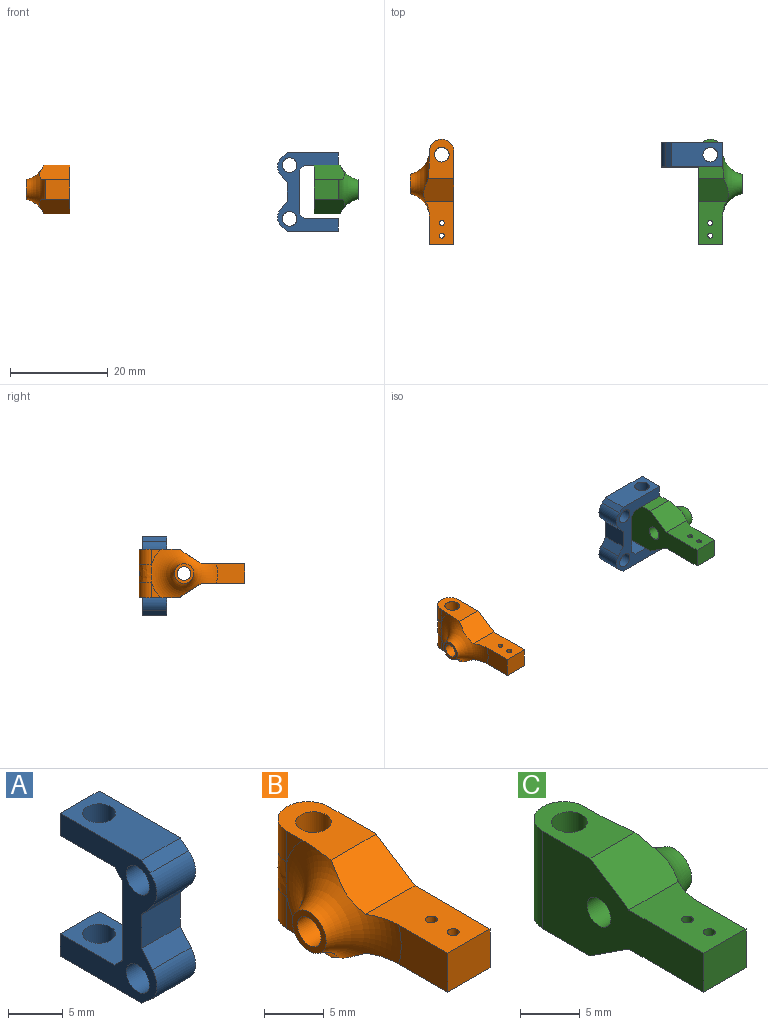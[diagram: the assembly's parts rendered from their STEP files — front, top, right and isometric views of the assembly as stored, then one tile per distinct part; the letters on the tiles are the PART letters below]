
ASSEMBLY  parts=3 mates=1
PART A: 22 faces, bbox 5x12.5x16 mm
  f0: plane 16x12.48mm, normal (1,0,0), area 82.5mm2, adj f2,f3,f4,f5,f6,f7,f8,f9
  f1: plane 16x12.48mm, normal (-1,0,0), area 82.5mm2, adj f2,f3,f4,f5,f6,f7,f8,f9
  f2: plane 5x3.79mm, normal (0,-1,0), area 18.9mm2, adj f0,f1,f14,f16
  f3: plane 9x5mm, normal (0,1,0), area 45mm2, adj f0,f1,f20,f21
  f4: plane 7x5mm, normal (0,0,-1), area 27.9mm2, adj f0,f1,f9,f11,f21
  f5: plane 10.5x5mm, normal (0,0,1), area 45.4mm2, adj f0,f1,f9,f11,f15
  f6: plane 10.5x5mm, normal (0,0,-1), area 45.4mm2, adj f0,f1,f8,f10,f12
  f7: plane 7x5mm, normal (0,0,1), area 27.9mm2, adj f0,f1,f8,f10,f20
  f8: plane 5x2.5mm, normal (0,1,0), area 12.5mm2, adj f0,f1,f6,f7
  f9: plane 5x2.5mm, normal (0,1,0), area 12.5mm2, adj f0,f1,f4,f5
  f10: cylinder r=1.5mm len=3mm, axis (0,0,1), area 23.6mm2, adj f6,f7
  f11: cylinder r=1.5mm len=3mm, axis (0,0,1), area 23.6mm2, adj f4,f5
  f12: plane 5x1.08mm, normal (0,-0.64,-0.77), area 7mm2, adj f0,f1,f6,f18
  f13: cylinder r=1.5mm len=5mm, axis (1,0,0), area 47.1mm2, adj f0,f1
  f14: plane 5x1.69mm, normal (0,-0.77,0.64), area 11mm2, adj f0,f1,f2,f18
  f15: plane 5x1.08mm, normal (0,-0.64,0.77), area 7mm2, adj f0,f1,f5,f19
  f16: plane 5x1.69mm, normal (0,-0.77,-0.64), area 11mm2, adj f0,f1,f2,f19
  f17: cylinder r=1.5mm len=5mm, axis (1,0,0), area 47.1mm2, adj f0,f1
  f18: cylinder r=2.5mm len=5mm, axis (1,0,0), area 19.6mm2, adj f0,f1,f12,f14
  f19: cylinder r=2.5mm len=5mm, axis (1,0,0), area 19.6mm2, adj f0,f1,f15,f16
  f20: plane 5x1mm, normal (0,0.71,0.71), area 7.1mm2, adj f0,f1,f3,f7
  f21: plane 5x1mm, normal (0,0.71,-0.71), area 7.1mm2, adj f0,f1,f3,f4
PART B: 20 faces, bbox 10.1x23.8x22.7 mm
  f0: plane 3.21x1.91mm, normal (-1,0,0), area 2.4mm2, adj f2,f17,f18
  f1: plane 3.21x1.91mm, normal (-1,0,0), area 2.4mm2, adj f4,f17,f18
  f2: plane 8.11x5.33mm, normal (0,0,1), area 31.3mm2, adj f0,f5,f8,f10,f17,f18
  f3: plane 5x4mm, normal (0,-1,0), area 20mm2, adj f5,f6,f9,f11
  f4: plane 8.11x5.33mm, normal (0,0,-1), area 31.3mm2, adj f1,f5,f8,f12,f17,f18
  f5: plane 19.09x10mm, normal (1,0,0), area 117.6mm2, adj f2,f3,f4,f7,f9,f10,f11,f12
  f6: plane 5.82x4mm, normal (-1,0,0), area 22.5mm2, adj f3,f9,f11,f17
  f7: cylinder r=1.4mm len=9mm, axis (-1,0,0), area 79.2mm2, adj f5,f16
  f8: cylinder r=1.5mm len=10mm, axis (0,0,1), area 94.2mm2, adj f2,f4
  f9: plane 8.89x5.88mm, normal (0,0,1), area 43.7mm2, adj f3,f5,f6,f10,f14,f15,f17
  f10: plane 6.24x4.6mm, normal (0,-0.55,0.84), area 32.6mm2, adj f2,f5,f9,f17
  f11: plane 8.89x5.88mm, normal (0,0,-1), area 43.7mm2, adj f3,f5,f6,f12,f14,f15,f17
  f12: plane 6.33x4.69mm, normal (0,-0.55,-0.84), area 32.6mm2, adj f4,f5,f11,f17
  f13: plane 3.58x0mm, normal (0,1,0), area 0mm2, adj f18,f19
  f14: cylinder r=0.5mm len=4mm, axis (0,0,1), area 12.6mm2, adj f9,f11
  f15: cylinder r=0.5mm len=4mm, axis (0,0,1), area 12.6mm2, adj f9,f11
  f16: plane 4x4mm, normal (-1,0,0), area 6.4mm2, adj f7,f17
  f17: torus R=6.9mm, axis (1,0,0), area 115.5mm2, adj f0,f1,f2,f4,f6,f9,f10,f11
  f18: cylinder r=2.5mm len=10mm, axis (0,0,-1), area 64.5mm2, adj f0,f1,f2,f4,f5,f13,f19
  f19: bspline ~6.96x2.7mm, area 13.9mm2, adj f13,f17,f18
PART C: 20 faces, bbox 10.1x23.8x22.7 mm
  f0: plane 3.21x1.91mm, normal (1,0,0), area 2.4mm2, adj f2,f17,f18
  f1: plane 3.21x1.91mm, normal (1,0,0), area 2.4mm2, adj f4,f17,f18
  f2: plane 8.11x5.33mm, normal (0,0,1), area 31.3mm2, adj f0,f5,f8,f10,f17,f18
  f3: plane 5x4mm, normal (0,-1,0), area 20mm2, adj f5,f6,f9,f11
  f4: plane 8.11x5.33mm, normal (0,0,-1), area 31.3mm2, adj f1,f5,f8,f12,f17,f18
  f5: plane 19.09x10mm, normal (-1,0,0), area 117.6mm2, adj f2,f3,f4,f7,f9,f10,f11,f12
  f6: plane 5.82x4mm, normal (1,0,0), area 22.5mm2, adj f3,f9,f11,f17
  f7: cylinder r=1.4mm len=9mm, axis (1,0,0), area 79.2mm2, adj f5,f16
  f8: cylinder r=1.5mm len=10mm, axis (0,0,1), area 94.2mm2, adj f2,f4
  f9: plane 8.89x5.88mm, normal (0,0,1), area 43.7mm2, adj f3,f5,f6,f10,f14,f15,f17
  f10: plane 6.24x4.6mm, normal (0,-0.55,0.84), area 32.6mm2, adj f2,f5,f9,f17
  f11: plane 8.89x5.88mm, normal (0,0,-1), area 43.7mm2, adj f3,f5,f6,f12,f14,f15,f17
  f12: plane 6.33x4.69mm, normal (0,-0.55,-0.84), area 32.6mm2, adj f4,f5,f11,f17
  f13: plane 3.58x0mm, normal (0,1,0), area 0mm2, adj f18,f19
  f14: cylinder r=0.5mm len=4mm, axis (0,0,1), area 12.6mm2, adj f9,f11
  f15: cylinder r=0.5mm len=4mm, axis (0,0,1), area 12.6mm2, adj f9,f11
  f16: plane 4x4mm, normal (1,0,0), area 6.4mm2, adj f7,f17
  f17: torus R=6.9mm, axis (-1,0,0), area 115.5mm2, adj f0,f1,f2,f4,f6,f9,f10,f11
  f18: cylinder r=2.5mm len=10mm, axis (0,0,-1), area 64.5mm2, adj f0,f1,f2,f4,f5,f13,f19
  f19: bspline ~6.96x2.7mm, area 13.9mm2, adj f13,f17,f18
PLACE A rot(axis=(0,0,-1),90deg) t=(32.51,9.3,-10.87)mm
PLACE B t=(-19.49,0.8,-10.37)mm
PLACE C t=(-19.49,0.8,-10.37)mm
MATE parallel A.f10 <-> C.f8  axis (0,0,-1) through (38.01,6.8,-5.37)mm
